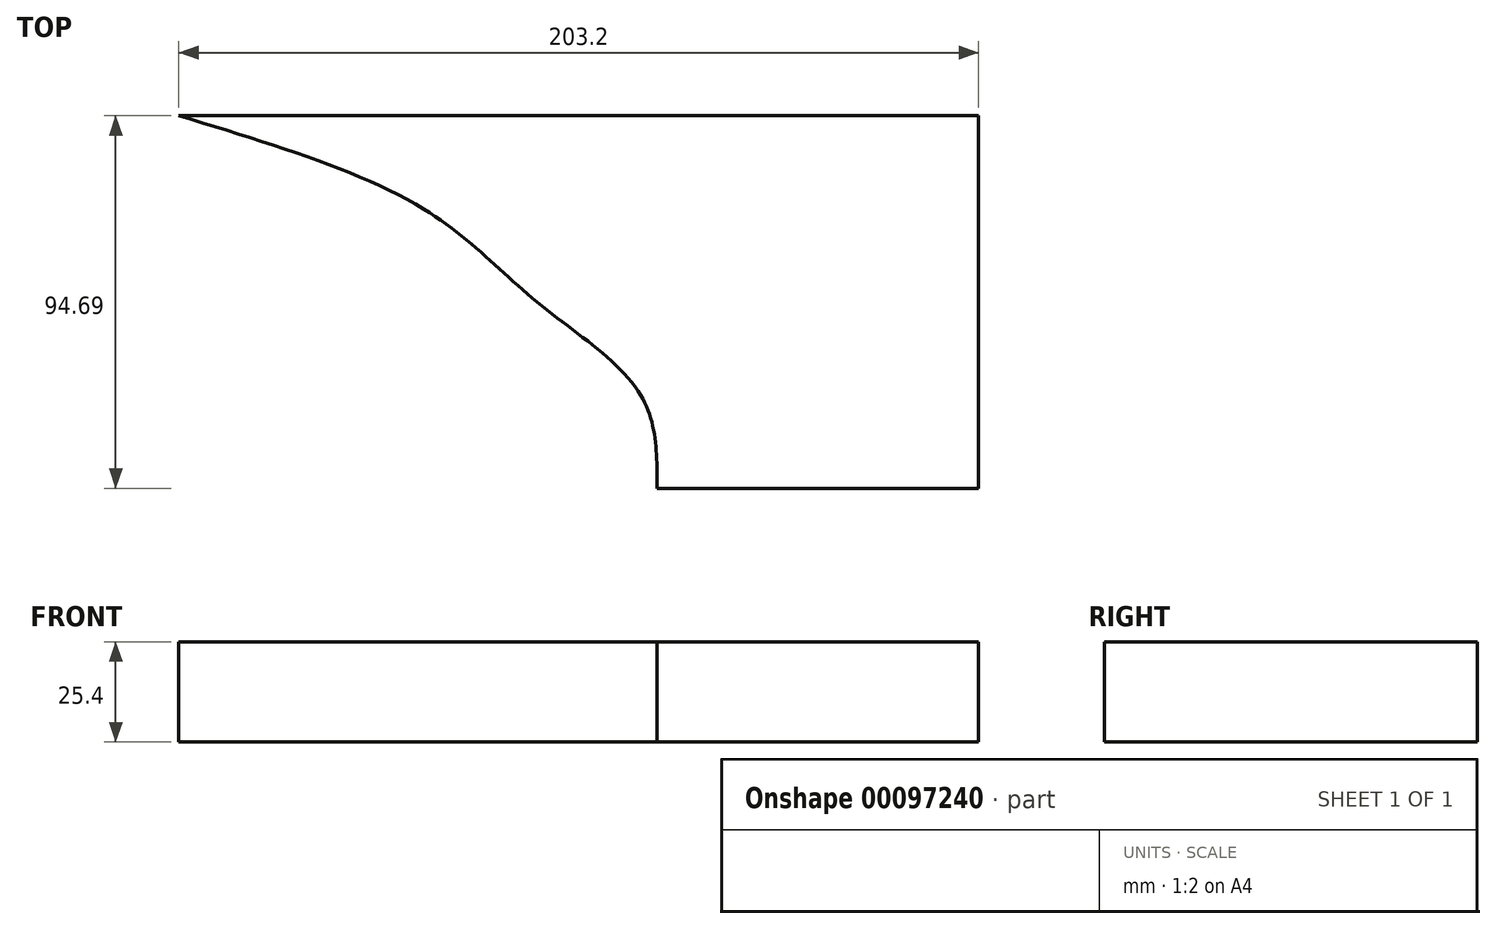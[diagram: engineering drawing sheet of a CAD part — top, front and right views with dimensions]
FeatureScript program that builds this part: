
annotation { "Feature Type Name" : "Feature", "Feature Type Description" : "" }
export const myFeature = defineFeature(function(context is Context, id is Id, definition is map)
    precondition{}
    {
        {
            var Q0;
            Q0=qCreatedBy(makeId("Top.planeOp"),FACE);
            var sketch = newSketch(context, id + "F0", { "sketchPlane" : qUnion([Q0])});
            skCircle(sketch, "E0", {"center": v(0, 0) * mm, "radius": 152.4 * mm});
            skLineSegment(sketch, "E1", {"start": v(0, 0) * mm, "end": v(0, 152.4) * mm, "construction": true});
            skLineSegment(sketch, "E2", {"start": v(0, 152.4) * mm, "end": v(203.2, 152.4) * mm, "construction": true});
            skLineSegment(sketch, "E3", {"start": v(203.2, 152.4) * mm, "end": v(203.2, 122.24) * mm, "construction": true});
            skLineSegment(sketch, "E4", {"start": v(203.2, 122.24) * mm, "end": v(203.2, 92.08) * mm, "construction": true});
            skCircle(sketch, "E5", {"center": v(203.2, 122.24) * mm, "radius": 30.16 * mm});
            skCircle(sketch, "E6", {"center": v(203.2, 152.4) * mm, "radius": 35.87 * mm, "construction": true});
            skCircle(sketch, "E7", {"center": v(233.36, 122.24) * mm, "radius": 24.47 * mm, "construction": true});
            skCircle(sketch, "E8", {"center": v(203.2, 92.08) * mm, "radius": 30.16 * mm, "construction": true});
            skLineSegment(sketch, "E9", {"start": v(203.2, 122.24) * mm, "end": v(238.52, 146.15) * mm, "construction": true});
            skLineSegment(sketch, "E10", {"start": v(203.2, 122.24) * mm, "end": v(231.2, 80.88) * mm, "construction": true});
            skLineSegment(sketch, "E11", {"start": v(203.2, 92.08) * mm, "end": v(121.44, 92.08) * mm, "construction": true});
            skLineSegment(sketch, "E12", {"start": v(220.11, 97.26) * mm, "end": v(117.33, 97.26) * mm, "construction": true});
            skLineSegment(sketch, "E13", {"start": v(203.2, 122.24) * mm, "end": v(91.02, 122.24) * mm, "construction": true});
            skLineSegment(sketch, "E14", {"start": v(228.18, 139.15) * mm, "end": v(62.16, 139.15) * mm, "construction": true});
            skLineSegment(sketch, "E15", {"start": v(203.2, 152.4) * mm, "end": v(203.2, 260.9) * mm, "construction": true});
            skLineSegment(sketch, "E16", {"start": v(203.2, 260.9) * mm, "end": v(121.44, 260.9) * mm});
            skLineSegment(sketch, "E17", {"start": v(203.2, 260.9) * mm, "end": v(203.2, 284.58) * mm});
            skLineSegment(sketch, "E18", {"start": v(203.2, 284.58) * mm, "end": v(117.33, 284.58) * mm});
            skLineSegment(sketch, "E19", {"start": v(203.2, 284.58) * mm, "end": v(203.2, 308.25) * mm});
            skLineSegment(sketch, "E20", {"start": v(203.2, 308.25) * mm, "end": v(91.02, 308.25) * mm});
            skLineSegment(sketch, "E21", {"start": v(203.2, 308.25) * mm, "end": v(203.2, 331.93) * mm});
            skLineSegment(sketch, "E22", {"start": v(203.2, 331.93) * mm, "end": v(62.16, 331.93) * mm});
            skLineSegment(sketch, "E23", {"start": v(203.2, 331.93) * mm, "end": v(203.2, 355.6) * mm});
            skLineSegment(sketch, "E24", {"start": v(203.2, 355.6) * mm, "end": v(0, 355.6) * mm});
            skLineSegment(sketch, "E25.MirrorCS", {"start": v(203.2, 426.62) * mm, "end": v(117.33, 426.62) * mm});
            skLineSegment(sketch, "E26.MirrorCS", {"start": v(203.2, 402.95) * mm, "end": v(91.02, 402.95) * mm});
            skLineSegment(sketch, "E27.MirrorCS", {"start": v(203.2, 379.27) * mm, "end": v(203.2, 355.6) * mm});
            skLineSegment(sketch, "E28.MirrorCS", {"start": v(203.2, 379.27) * mm, "end": v(62.16, 379.27) * mm});
            skLineSegment(sketch, "E29.MirrorCS", {"start": v(203.2, 450.3) * mm, "end": v(203.2, 426.62) * mm});
            skLineSegment(sketch, "E30.MirrorCS", {"start": v(203.2, 402.95) * mm, "end": v(203.2, 379.27) * mm});
            skLineSegment(sketch, "E31.MirrorCS", {"start": v(203.2, 426.62) * mm, "end": v(203.2, 402.95) * mm});
            skLineSegment(sketch, "E32.MirrorCS", {"start": v(203.2, 450.3) * mm, "end": v(121.44, 450.3) * mm});
            skFitSpline(sketch, "E33", {"points": [v(121.44, 260.9) * mm, v(117.33, 284.58) * mm, v(91.02, 308.25) * mm, v(62.16, 331.93) * mm, v(0, 355.6) * mm], "startDerivative": vector(1.33, 126.66) * mm, "endDerivative": vector(-214.92, 65.23) * mm});
            skSolve(sketch);
        }
        {
            var Q0;
            {var subQ0=sQuery(id+"F0.wireOp",EDGE,"E25.MirrorCS");Q0=makeQuery(id+"F0.imprint","IMPRINT",FACE,{"disambiguationData":[TD([[makeQuery(id+"F0.imprint","IMPRINT",EDGE,{"derivedFrom":subQ0}),-1.0]])]});}
            var Q1;
            {var subQ0=sQuery(id+"F0.wireOp",EDGE,"E25.MirrorCS");Q1=makeQuery(id+"F0.imprint","IMPRINT",FACE,{"disambiguationData":[TD([[makeQuery(id+"F0.imprint","IMPRINT",EDGE,{"derivedFrom":subQ0}),1.0]])]});}
            var Q2;
            {var subQ0=sQuery(id+"F0.wireOp",EDGE,"E26.MirrorCS");Q2=makeQuery(id+"F0.imprint","IMPRINT",FACE,{"disambiguationData":[TD([[makeQuery(id+"F0.imprint","IMPRINT",EDGE,{"derivedFrom":subQ0}),1.0]])]});}
            var Q3;
            {var subQ0=sQuery(id+"F0.wireOp",EDGE,"E24");Q3=makeQuery(id+"F0.imprint","IMPRINT",FACE,{"disambiguationData":[TD([[makeQuery(id+"F0.imprint","IMPRINT",EDGE,{"derivedFrom":subQ0}),-1.0]])]});}
            var Q4;
            {var subQ0=sQuery(id+"F0.wireOp",EDGE,"E22");Q4=makeQuery(id+"F0.imprint","IMPRINT",FACE,{"disambiguationData":[TD([[makeQuery(id+"F0.imprint","IMPRINT",EDGE,{"derivedFrom":subQ0}),-1.0]])]});}
            var Q5;
            {var subQ0=sQuery(id+"F0.wireOp",EDGE,"E20");Q5=makeQuery(id+"F0.imprint","IMPRINT",FACE,{"disambiguationData":[TD([[makeQuery(id+"F0.imprint","IMPRINT",EDGE,{"derivedFrom":subQ0}),-1.0]])]});}
            var Q6;
            {var subQ0=sQuery(id+"F0.wireOp",EDGE,"E18");Q6=makeQuery(id+"F0.imprint","IMPRINT",FACE,{"disambiguationData":[TD([[makeQuery(id+"F0.imprint","IMPRINT",EDGE,{"derivedFrom":subQ0}),-1.0]])]});}
            var Q7;
            {var subQ0=sQuery(id+"F0.wireOp",EDGE,"E16");Q7=makeQuery(id+"F0.imprint","IMPRINT",FACE,{"disambiguationData":[TD([[makeQuery(id+"F0.imprint","IMPRINT",EDGE,{"derivedFrom":subQ0}),-1.0]])]});}
            extrude(context, id + "F1", {"entities" : qUnion([Q0, Q1, Q2, Q3, Q4, Q5, Q6, Q7]), "depth" : 25.4 * mm});
        }
    });
